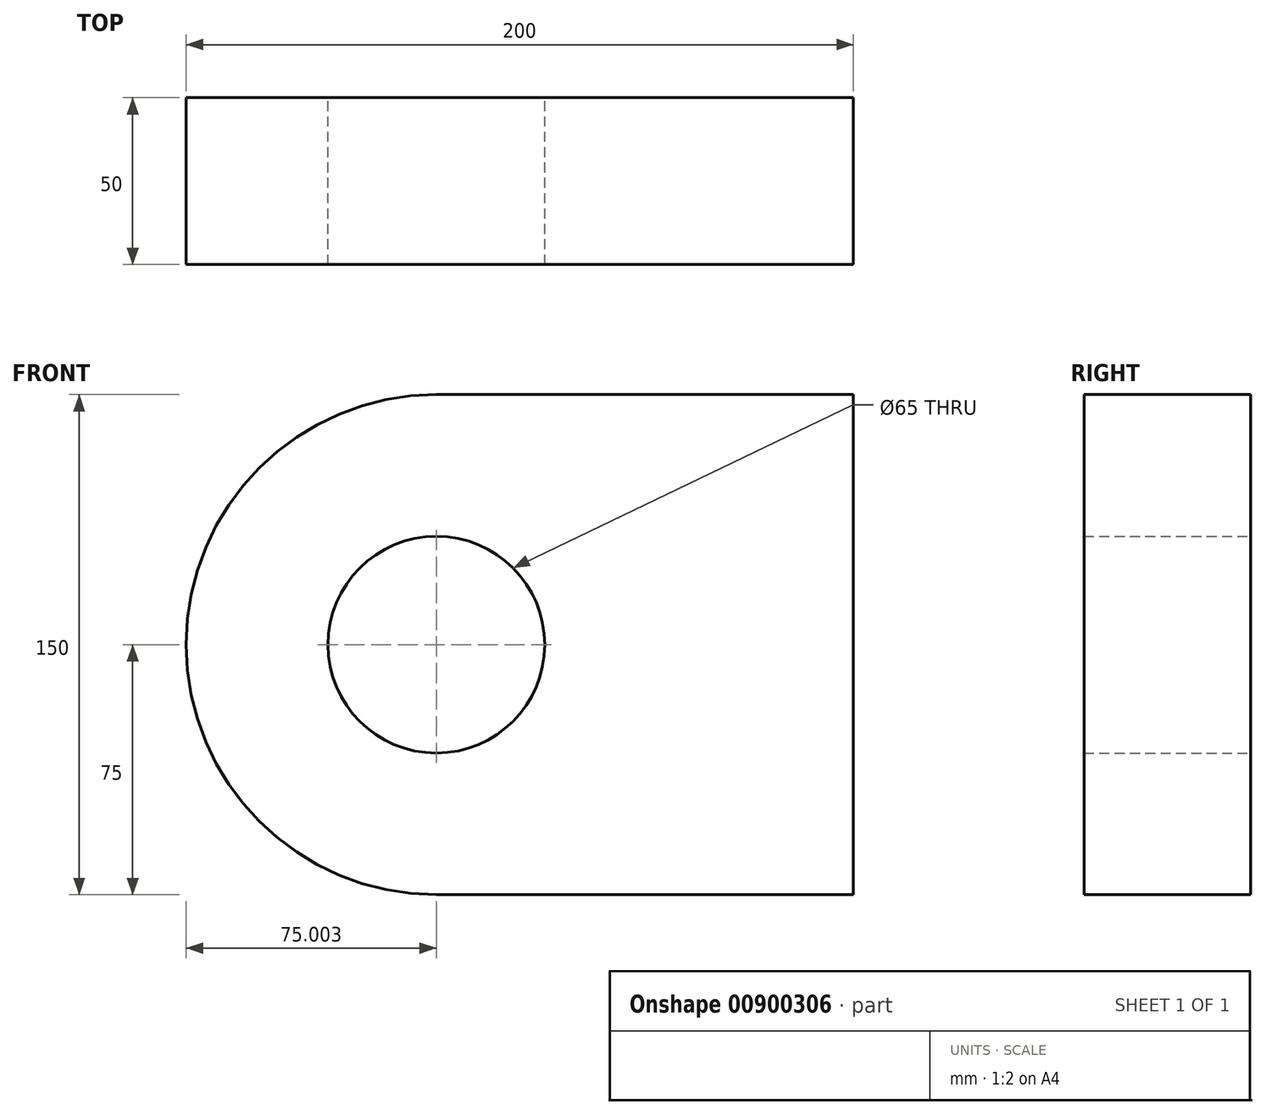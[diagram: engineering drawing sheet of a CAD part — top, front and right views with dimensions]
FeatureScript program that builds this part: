
annotation { "Feature Type Name" : "Feature", "Feature Type Description" : "" }
export const myFeature = defineFeature(function(context is Context, id is Id, definition is map)
    precondition{}
    {
        {
            var Q0;
            Q0=qCreatedBy(makeId("Front.planeOp"),FACE);
            var sketch = newSketch(context, id + "F0", { "sketchPlane" : qUnion([Q0])});
            skLineSegment(sketch, "E0.right", {"start": v(-395.8, 146.1) * mm, "end": v(-395.8, -53.9) * mm});
            skLineSegment(sketch, "E1.top", {"start": v(-395.8, 121.1) * mm, "end": v(-520.8, 121.1) * mm});
            skLineSegment(sketch, "E1.left", {"start": v(-395.8, 46.1) * mm, "end": v(-395.8, 121.1) * mm});
            skLineSegment(sketch, "E1.right", {"start": v(-595.8, 46.1) * mm, "end": v(-595.8, 46.1) * mm});
            skLineSegment(sketch, "E2.MirrorCS", {"start": v(-395.8, -28.9) * mm, "end": v(-520.8, -28.9) * mm});
            skLineSegment(sketch, "E3.MirrorCS", {"start": v(-395.8, 46.1) * mm, "end": v(-395.8, -28.9) * mm});
            skPoint(sketch, "E4.visualSharp", {"position": v(-595.8, 121.1) * mm});
            skArc(sketch, "E4.filletArc", {"start": v(-520.8, 121.1) * mm, "mid": v(-573.83, 99.14) * mm, "end": v(-595.8, 46.1) * mm});
            skPoint(sketch, "E5.visualSharp", {"position": v(-595.8, -28.9) * mm});
            skArc(sketch, "E5.filletArc", {"start": v(-595.8, 46.1) * mm, "mid": v(-573.83, -6.92) * mm, "end": v(-520.8, -28.9) * mm});
            skCircle(sketch, "E6", {"center": v(-520.8, 46.1) * mm, "radius": 32.5 * mm});
            skSolve(sketch);
        }
        {
            var Q0;
            Q0 = qSketchRegion(id + "F0", true);
            var Q1;
            Q1=makeQuery(id+"F0.imprint","IMPRINT",FACE,{"disambiguationData":[TD([[makeQuery(id+"F0.imprint","IMPRINT",EDGE,{"derivedFrom":sQuery(id+"F0.wireOp",EDGE,"E1.top")}),1.0]])]});
            extrude(context, id + "F1", {"entities" : qUnion([Q0, Q1]), "depth" : 50 * mm, "offsetDistance" : 25 * mm});
        }
    });
